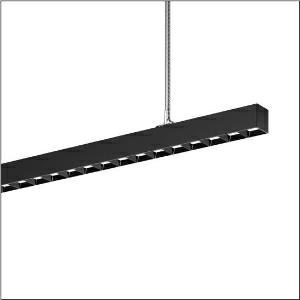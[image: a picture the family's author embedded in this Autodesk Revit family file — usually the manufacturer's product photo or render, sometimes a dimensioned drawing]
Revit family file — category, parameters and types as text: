
# Revit family: silica_r__21_51mx32dc3dbb_53cb
name_source: partatom
category: Lighting Fixtures
units: mm (PartAtom-declared; Revit-internal decimal feet)

## family parameters
Cut with Voids When Loaded = No
Host = Face
Light Source = No
Part Type = Normal
Room Calculation Point = No
Round Connector Dimension = Use Diameter
Shared = No

## types (1)
- --- (1 x LED, 18220 lm, 113 W, 3000K)
    Apparent Load = 113 VA
    CIE Flux Codes = 86 99 100 59 100
    Color Rendering = 80
    Color Temperature = 3000K
    Default Elevation = 1800 mm
    Description = Silica® 21, office luminaire, primary light control with darklight reflector, of PMMA, black, CAT 2 (L<= 3000cd/m²), light emission: direct/indirect distribution, primary light characteristic: symmetric, installation type: suspended mounting, LED, rated luminous flux: 18.220lm, luminous efficacy: 161lm/W, light colour: 830, colour temperature: 3000K, with terminal, 3+2-pole, max. 2.5mm², mains connection: 220..240V, AC, 50/60Hz, rated input power: 113W, luminaire housing, of aluminium, jet black (RAL 9005), length: 3.004mm, width: 53mm, height: 53mm, protection rating (complete): IP20, insulation class (complete): insulation class I (protective earthing), certification: CE, permissible operating ambient temperature: 0..+35°C, standard: EN 50419, packaging unit: 1 piece
    Height = 53 mm
    Lamp = 1 x LED
    Lamp Light Flux = 18220 lm
    Lamp Power = 113 W
    Lamp count = 1
    Length = 3004 mm
    Luminous efficacy = 161 lm/W
    Manufacturer = Siteco
    ModVariant = No
    Model = 51MX32DC3DBB
    Mounting Place = Ceiling
    Mounting Type = Pendant
    Number of Poles = 1
    OnlyDefault = Yes
    Power Factor = 1
    Product Name = Silica® 21
    Product group = office luminaire | ceiling pendant
    ProductGroupID = 902
    Protection Class = Protection class I
    Protection Degree = IP 20
    RLX_Detail_Level = 1
    RLX_Emergency_Light_Flux = 0 lm
    RLX_Emergency_Type = 0
    RLX_Emergency_Type_DB = No
    RlxData = <blob elided: 66897 chars, md5=9c547b2d>
    Socket = socket
    Standby Power = 0 W
    System Light Flux = 18220 lm
    System Power = 113 W
    Type Comments = factory setting: luminous flux: 100 % | dim-lin: 254 | 391 mA
    Type Image = l_1313617.jpg
    URL = http://relux.com
    VarID = @adj_070921
    Voltage = 0 V
    Weight = 0.00 kg
    Width = 53 mm

## geometry (parser evidence)
native form markers: Blend x4, Sweep x11
no freeform markers — native parametric forms only
